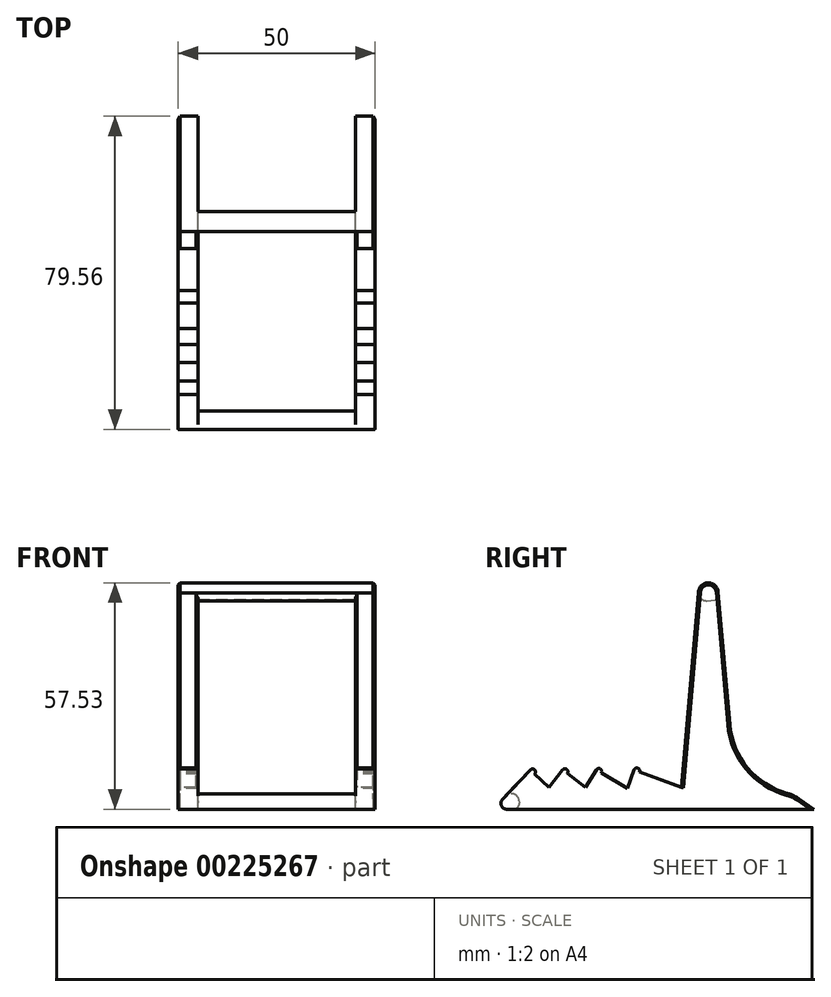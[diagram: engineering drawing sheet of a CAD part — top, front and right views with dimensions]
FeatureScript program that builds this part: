
annotation { "Feature Type Name" : "Feature", "Feature Type Description" : "" }
export const myFeature = defineFeature(function(context is Context, id is Id, definition is map)
    precondition{}
    {
        {
            var Q0;
            Q0=qCreatedBy(makeId("Right.planeOp"),FACE);
            var sketch = newSketch(context, id + "F0", { "sketchPlane" : qUnion([Q0])});
            skLineSegment(sketch, "E0", {"start": v(30, 0.35) * mm, "end": v(25.63, 50.25) * mm});
            skLineSegment(sketch, "E1", {"start": v(20.64, 50) * mm, "end": v(16.7, 5) * mm});
            skLineSegment(sketch, "E2", {"start": v(20.64, 50) * mm, "end": v(-21.34, -65.34) * mm, "construction": true});
            skLineSegment(sketch, "E3", {"start": v(-41.86, -58.25) * mm, "end": v(20.64, 50) * mm, "construction": true});
            skLineSegment(sketch, "E4", {"start": v(20.64, 50) * mm, "end": v(-56.77, -50.88) * mm, "construction": true});
            skLineSegment(sketch, "E5", {"start": v(-69.14, -44.61) * mm, "end": v(20.64, 50) * mm, "construction": true});
            skLineSegment(sketch, "E6", {"start": v(-49.53, 5) * mm, "end": v(47.68, 5) * mm, "construction": true});
            skArc(sketch, "E7", {"start": v(25.63, 50.25) * mm, "mid": v(23.02, 52.53) * mm, "end": v(20.64, 50) * mm});
            skLineSegment(sketch, "E8", {"start": v(-22.06, 5) * mm, "end": v(-17.33, 0.51) * mm});
            skLineSegment(sketch, "E9", {"start": v(-17.33, 0.51) * mm, "end": v(-13.89, 5) * mm});
            skLineSegment(sketch, "E10", {"start": v(-13.89, 5) * mm, "end": v(-8.04, 0.51) * mm});
            skLineSegment(sketch, "E11", {"start": v(-8.04, 0.51) * mm, "end": v(-5.34, 5) * mm});
            skLineSegment(sketch, "E12", {"start": v(-5.34, 5) * mm, "end": v(2.54, 0.26) * mm});
            skLineSegment(sketch, "E13", {"start": v(2.54, 0.26) * mm, "end": v(4.27, 5) * mm});
            skLineSegment(sketch, "E14", {"start": v(-31.55, -5) * mm, "end": v(50, -5) * mm});
            skLineSegment(sketch, "E15", {"start": v(50, -5) * mm, "end": v(44.6, -1.3) * mm});
            skLineSegment(sketch, "E16", {"start": v(-22.06, 5) * mm, "end": v(-31.55, -5) * mm});
            skLineSegment(sketch, "E17", {"start": v(4.27, 5) * mm, "end": v(16.32, 0.61) * mm});
            skLineSegment(sketch, "E18", {"start": v(16.7, 5) * mm, "end": v(16.32, 0.61) * mm});
            skArc(sketch, "E19", {"start": v(-20.97, 3.97) * mm, "mid": v(-21, 5.03) * mm, "end": v(-22.06, 5) * mm});
            skArc(sketch, "E20", {"start": v(-12.7, 4.09) * mm, "mid": v(-12.83, 5.14) * mm, "end": v(-13.89, 5) * mm});
            skArc(sketch, "E21", {"start": v(-4.05, 4.23) * mm, "mid": v(-4.3, 5.26) * mm, "end": v(-5.34, 5) * mm});
            skArc(sketch, "E22", {"start": v(5.68, 4.49) * mm, "mid": v(5.23, 5.45) * mm, "end": v(4.27, 5) * mm});
            skLineSegment(sketch, "E23", {"start": v(44.6, -1.3) * mm, "end": v(30, 0.35) * mm});
            skSolve(sketch);
        }
        {
            var Q0;
            Q0 = qSketchRegion(id + "F0", true);
            extrude(context, id + "F1", {"entities" : qUnion([Q0]), "depth" : 25 * mm, "offsetDistance" : 25 * mm, "hasSecondDirection" : true, "secondDirectionOppositeDirection" : true, "secondDirectionDepth" : 25 * mm});
        }
        {
            var Q0;
            Q0=makeQuery(id+"F1.opExtrude","SWEPT_FACE",FACE,{"disambiguationData":[OSD([sQuery(id+"F0.wireOp",EDGE,"E0")])]});
            var sketch = newSketch(context, id + "F2", { "sketchPlane" : qUnion([Q0])});
            skLineSegment(sketch, "E24.bottom", {"start": v(-20, 45.82) * mm, "end": v(20, 45.82) * mm});
            skLineSegment(sketch, "E24.top", {"start": v(-20, -9.34) * mm, "end": v(20, -9.34) * mm});
            skLineSegment(sketch, "E24.left", {"start": v(-20, 45.82) * mm, "end": v(-20, -9.34) * mm});
            skLineSegment(sketch, "E24.right", {"start": v(20, 45.82) * mm, "end": v(20, -9.34) * mm});
            skSolve(sketch);
        }
        {
            var Q0;
            Q0 = qSketchRegion(id + "F2", true);
            extrude(context, id + "F3", {"entities" : qUnion([Q0]), "operationType" : NewBodyOperationType.REMOVE, "oppositeDirection" : true, "depth" : 55 * mm, "offsetDistance" : 25 * mm, "hasSecondDirection" : true, "secondDirectionOppositeDirection" : false, "secondDirectionDepth" : 25 * mm});
        }
        {
            var Q0;
            Q0=makeQuery(id+"F3.boolean.opBoolean","INTERSECT",EDGE,{"derivedFrom":[makeQuery(id+"F1.opExtrude","SWEPT_FACE",FACE,{"disambiguationData":[OSD([sQuery(id+"F0.wireOp",EDGE,"E16")])]}),makeQuery(id+"F3.opExtrude","CAP_FACE",FACE,{"disambiguationData":[OSD([sQuery(id+"F2.wireOp",EDGE,"E24.bottom"),sQuery(id+"F2.wireOp",EDGE,"E24.top"),sQuery(id+"F2.wireOp",EDGE,"E24.left"),sQuery(id+"F2.wireOp",EDGE,"E24.right")])],"isStart":false})]});
            var Q1;
            Q1=makeQuery(id+"F3.boolean.opBoolean","COPY",EDGE,{"derivedFrom":makeQuery(id+"F3.opExtrude","CAP_EDGE",EDGE,{"disambiguationData":[OSD([sQuery(id+"F2.wireOp",EDGE,"E24.bottom")])],"isStart":true})});
            var Q2;
            Q2=makeQuery(id+"F3.boolean.opBoolean","INTERSECT",EDGE,{"derivedFrom":[makeQuery(id+"F1.opExtrude","SWEPT_FACE",FACE,{"disambiguationData":[OSD([sQuery(id+"F0.wireOp",EDGE,"E1"),sQuery(id+"F0.wireOp",EDGE,"E18")])]}),makeQuery(id+"F3.opExtrude","SWEPT_FACE",FACE,{"disambiguationData":[OSD([sQuery(id+"F2.wireOp",EDGE,"E24.bottom")])]})]});
            fillet(context, id + "F4", {"entities" : qUnion([Q0, Q1, Q2]), "radius" : 2 * mm, "tangentPropagation" : true, "allowEdgeOverflow" : false});
        }
        {
            var Q0;
            Q0=makeQuery(id+"F1.opExtrude","SWEPT_EDGE",EDGE,{"disambiguationData":[OSD([sQuery(id+"F0.wireOp",EDGE,"E14"),sQuery(id+"F0.wireOp",EDGE,"E16")])]});
            var Q1;
            Q1=makeQuery(id+"F3.boolean.opBoolean","INTERSECT",EDGE,{"derivedFrom":[makeQuery(id+"F1.opExtrude","SWEPT_FACE",FACE,{"disambiguationData":[OSD([sQuery(id+"F0.wireOp",EDGE,"E14")])]}),makeQuery(id+"F3.opExtrude","CAP_FACE",FACE,{"disambiguationData":[OSD([sQuery(id+"F2.wireOp",EDGE,"E24.bottom"),sQuery(id+"F2.wireOp",EDGE,"E24.top"),sQuery(id+"F2.wireOp",EDGE,"E24.left"),sQuery(id+"F2.wireOp",EDGE,"E24.right")])],"isStart":false})]});
            fillet(context, id + "F5", {"entities" : qUnion([Q0, Q1]), "radius" : 1.5 * mm, "tangentPropagation" : true, "allowEdgeOverflow" : false});
        }
        {
            var Q0;
            {var subQ0=sQuery(id+"F0.wireOp",EDGE,"E0");var subQ1=sQuery(id+"F0.wireOp",EDGE,"E23");Q0=makeQuery(id+"F3.boolean.opBoolean","SPLIT",EDGE,{"disambiguationData":[TD([makeQuery(id+"F3.opExtrude","SWEPT_FACE",FACE,{"disambiguationData":[OSD([sQuery(id+"F2.wireOp",EDGE,"E24.left")])]})])],"derivedFrom":makeQuery(id+"F1.opExtrude","SWEPT_EDGE",EDGE,{"disambiguationData":[OSD([subQ0,subQ1])]})});}
            var Q1;
            {var subQ0=sQuery(id+"F0.wireOp",EDGE,"E0");var subQ1=sQuery(id+"F0.wireOp",EDGE,"E23");Q1=makeQuery(id+"F3.boolean.opBoolean","SPLIT",EDGE,{"disambiguationData":[TD([makeQuery(id+"F3.opExtrude","SWEPT_FACE",FACE,{"disambiguationData":[OSD([sQuery(id+"F2.wireOp",EDGE,"E24.right")])]})])],"derivedFrom":makeQuery(id+"F1.opExtrude","SWEPT_EDGE",EDGE,{"disambiguationData":[OSD([subQ0,subQ1])]})});}
            fillet(context, id + "F6", {"entities" : qUnion([Q0, Q1]), "radius" : 20 * mm, "tangentPropagation" : true, "allowEdgeOverflow" : false});
        }
        {
            var Q0;
            {var subQ0=sQuery(id+"F0.wireOp",EDGE,"E23");var subQ1=sQuery(id+"F0.wireOp",EDGE,"E15");var subQ3=sQuery(id+"F0.wireOp",EDGE,"E0");var subQ6=makeQuery(id+"F3.opExtrude","SWEPT_FACE",FACE,{"disambiguationData":[OSD([sQuery(id+"F2.wireOp",EDGE,"E24.left")])]});Q0=makeQuery(id+"F6.opFillet","BLEND_EDGE",EDGE,{"blendedFrom":[makeQuery(id+"F3.boolean.opBoolean","SPLIT",EDGE,{"disambiguationData":[TD([subQ6])],"derivedFrom":makeQuery(id+"F1.opExtrude","SWEPT_EDGE",EDGE,{"disambiguationData":[OSD([subQ3,subQ0])]})}),makeQuery(id+"F3.boolean.opBoolean","SPLIT",FACE,{"disambiguationData":[TD([subQ6])],"derivedFrom":makeQuery(id+"F1.opExtrude","SWEPT_FACE",FACE,{"disambiguationData":[OSD([subQ1])]})})],"blendedInto":[makeQuery(id+"F3.boolean.opBoolean","SPLIT",FACE,{"disambiguationData":[TD([subQ6])],"derivedFrom":makeQuery(id+"F1.opExtrude","SWEPT_FACE",FACE,{"disambiguationData":[OSD([subQ1])]})})]});}
            var Q1;
            {var subQ0=sQuery(id+"F0.wireOp",EDGE,"E23");var subQ1=sQuery(id+"F0.wireOp",EDGE,"E15");var subQ3=sQuery(id+"F0.wireOp",EDGE,"E0");var subQ6=makeQuery(id+"F3.opExtrude","SWEPT_FACE",FACE,{"disambiguationData":[OSD([sQuery(id+"F2.wireOp",EDGE,"E24.right")])]});Q1=makeQuery(id+"F6.opFillet","BLEND_EDGE",EDGE,{"blendedFrom":[makeQuery(id+"F3.boolean.opBoolean","SPLIT",EDGE,{"disambiguationData":[TD([subQ6])],"derivedFrom":makeQuery(id+"F1.opExtrude","SWEPT_EDGE",EDGE,{"disambiguationData":[OSD([subQ3,subQ0])]})}),makeQuery(id+"F3.boolean.opBoolean","SPLIT",FACE,{"disambiguationData":[TD([subQ6])],"derivedFrom":makeQuery(id+"F1.opExtrude","SWEPT_FACE",FACE,{"disambiguationData":[OSD([subQ1])]})})],"blendedInto":[makeQuery(id+"F3.boolean.opBoolean","SPLIT",FACE,{"disambiguationData":[TD([subQ6])],"derivedFrom":makeQuery(id+"F1.opExtrude","SWEPT_FACE",FACE,{"disambiguationData":[OSD([subQ1])]})})]});}
            fillet(context, id + "F7", {"entities" : qUnion([Q0, Q1]), "radius" : 10 * mm, "tangentPropagation" : true, "allowEdgeOverflow" : false});
        }
        {
            var Q0;
            Q0=makeQuery(id+"F3.boolean.opBoolean","INTERSECT",EDGE,{"derivedFrom":[makeQuery(id+"F1.opExtrude","SWEPT_FACE",FACE,{"disambiguationData":[OSD([sQuery(id+"F0.wireOp",EDGE,"E1"),sQuery(id+"F0.wireOp",EDGE,"E18")])]}),makeQuery(id+"F3.opExtrude","SWEPT_FACE",FACE,{"disambiguationData":[OSD([sQuery(id+"F2.wireOp",EDGE,"E24.left")])]})]});
            var Q1;
            Q1=makeQuery(id+"F3.boolean.opBoolean","INTERSECT",EDGE,{"derivedFrom":[makeQuery(id+"F1.opExtrude","SWEPT_FACE",FACE,{"disambiguationData":[OSD([sQuery(id+"F0.wireOp",EDGE,"E1"),sQuery(id+"F0.wireOp",EDGE,"E18")])]}),makeQuery(id+"F3.opExtrude","SWEPT_FACE",FACE,{"disambiguationData":[OSD([sQuery(id+"F2.wireOp",EDGE,"E24.right")])]})]});
            var Q2;
            Q2=makeQuery(id+"F1.opExtrude","CAP_EDGE",EDGE,{"disambiguationData":[OSD([sQuery(id+"F0.wireOp",EDGE,"E1"),sQuery(id+"F0.wireOp",EDGE,"E18")])],"isStart":true});
            var Q3;
            Q3=makeQuery(id+"F1.opExtrude","CAP_EDGE",EDGE,{"disambiguationData":[OSD([sQuery(id+"F0.wireOp",EDGE,"E0")])],"isStart":true});
            var Q4;
            Q4=makeQuery(id+"F3.boolean.opBoolean","COPY",EDGE,{"derivedFrom":makeQuery(id+"F3.opExtrude","CAP_EDGE",EDGE,{"disambiguationData":[OSD([sQuery(id+"F2.wireOp",EDGE,"E24.right")])],"isStart":true})});
            var Q5;
            Q5=makeQuery(id+"F1.opExtrude","CAP_EDGE",EDGE,{"disambiguationData":[OSD([sQuery(id+"F0.wireOp",EDGE,"E0")])],"isStart":false});
            var Q6;
            Q6=makeQuery(id+"F3.boolean.opBoolean","COPY",EDGE,{"derivedFrom":makeQuery(id+"F3.opExtrude","CAP_EDGE",EDGE,{"disambiguationData":[OSD([sQuery(id+"F2.wireOp",EDGE,"E24.left")])],"isStart":true})});
            var Q7;
            Q7=makeQuery(id+"F1.opExtrude","CAP_EDGE",EDGE,{"disambiguationData":[OSD([sQuery(id+"F0.wireOp",EDGE,"E1"),sQuery(id+"F0.wireOp",EDGE,"E18")])],"isStart":false});
            chamfer(context, id + "F8", {"entities" : qUnion([Q0, Q1, Q2, Q3, Q4, Q5, Q6, Q7]), "width" : 0.5 * mm, "tangentPropagation" : true});
        }
    });
